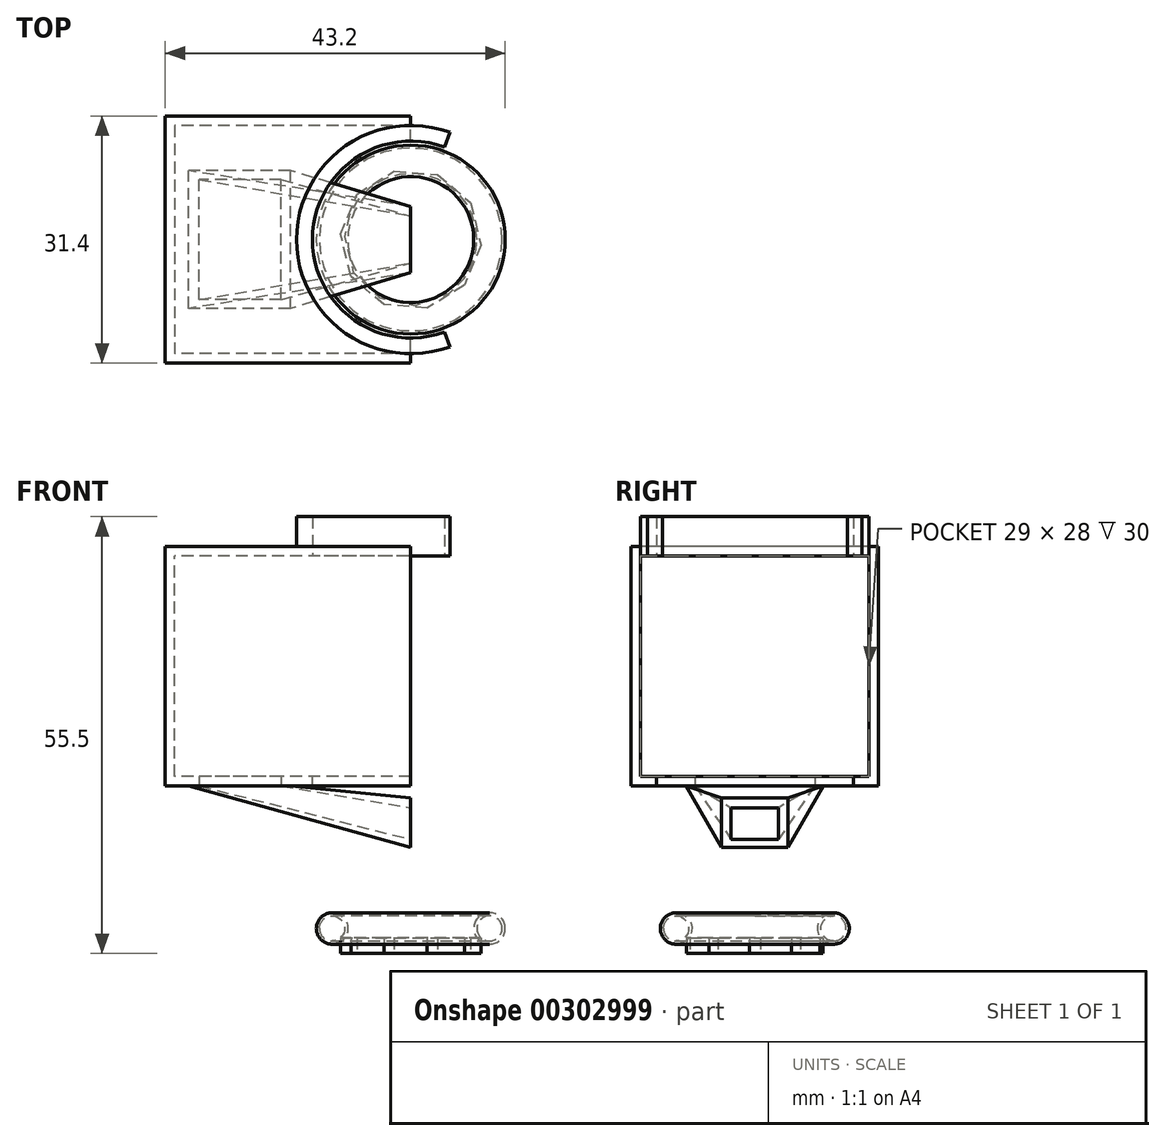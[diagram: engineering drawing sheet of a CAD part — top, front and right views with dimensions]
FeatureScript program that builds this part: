
annotation { "Feature Type Name" : "Feature", "Feature Type Description" : "" }
export const myFeature = defineFeature(function(context is Context, id is Id, definition is map)
    precondition{}
    {
        {
            var Q0;
            Q0=qCreatedBy(makeId("Top.planeOp"),FACE);
            var sketch = newSketch(context, id + "F0", { "sketchPlane" : qUnion([Q0])});
            skCircle(sketch, "E0", {"center": v(0, 0) * mm, "radius": 12.5 * mm});
            skCircle(sketch, "E1", {"center": v(0, 0) * mm, "radius": 14.5 * mm});
            skLineSegment(sketch, "E2.bottom", {"start": v(0, 14.5) * mm, "end": v(-30, 14.5) * mm});
            skLineSegment(sketch, "E2.top", {"start": v(0, -14.5) * mm, "end": v(-30, -14.5) * mm});
            skLineSegment(sketch, "E2.left", {"start": v(0, 14.5) * mm, "end": v(0, -14.5) * mm});
            skLineSegment(sketch, "E2.right", {"start": v(-30, 14.5) * mm, "end": v(-30, -14.5) * mm});
            skLineSegment(sketch, "E3.0", {"start": v(0, -15.7) * mm, "end": v(-31.2, -15.7) * mm});
            skLineSegment(sketch, "E3.1", {"start": v(-31.2, 15.7) * mm, "end": v(-31.2, -15.7) * mm});
            skLineSegment(sketch, "E3.2", {"start": v(0, 15.7) * mm, "end": v(-31.2, 15.7) * mm});
            skLineSegment(sketch, "E4", {"start": v(0, -15.7) * mm, "end": v(0, -14.5) * mm});
            skLineSegment(sketch, "E5", {"start": v(0, 14.5) * mm, "end": v(0, 15.7) * mm});
            skLineSegment(sketch, "E6", {"start": v(0, 0) * mm, "end": v(4.96, 13.63) * mm});
            skLineSegment(sketch, "E7", {"start": v(0, 0) * mm, "end": v(4.96, -13.63) * mm});
            skSolve(sketch);
        }
        {
            var Q0;
            {var subQ0=sQuery(id+"F0.wireOp",EDGE,"E2.left");var subQ1=sQuery(id+"F0.wireOp",EDGE,"E0");var subQ2=makeQuery(id+"F0.imprint","INTERSECT",VERTEX,{"disambiguationData":[OD(0.0)],"derivedFrom":[subQ1,subQ0]});Q0=makeQuery(id+"F0.imprint","IMPRINT",FACE,{"disambiguationData":[TD([[makeQuery(id+"F0.imprint","IMPRINT",EDGE,{"disambiguationData":[TD([[subQ2,-1.0]])],"derivedFrom":subQ1}),-1.0]])]});}
            var Q1;
            {var subQ0=sQuery(id+"F0.wireOp",EDGE,"E2.left");var subQ1=sQuery(id+"F0.wireOp",EDGE,"E0");var subQ2=makeQuery(id+"F0.imprint","INTERSECT",VERTEX,{"disambiguationData":[OD(0.0)],"derivedFrom":[subQ1,subQ0]});Q1=makeQuery(id+"F0.imprint","IMPRINT",FACE,{"disambiguationData":[TD([[makeQuery(id+"F0.imprint","IMPRINT",EDGE,{"disambiguationData":[TD([[subQ2,1.0]])],"derivedFrom":subQ1}),-1.0]])]});}
            var Q2;
            {var subQ0=sQuery(id+"F0.wireOp",EDGE,"E2.left");var subQ1=sQuery(id+"F0.wireOp",EDGE,"E0");var subQ2=makeQuery(id+"F0.imprint","INTERSECT",VERTEX,{"disambiguationData":[OD(1.0)],"derivedFrom":[subQ1,subQ0]});Q2=makeQuery(id+"F0.imprint","IMPRINT",FACE,{"disambiguationData":[TD([[makeQuery(id+"F0.imprint","IMPRINT",EDGE,{"disambiguationData":[TD([[subQ2,-1.0]])],"derivedFrom":subQ1}),-1.0]])]});}
            extrude(context, id + "F1", {"entities" : qUnion([Q0, Q1, Q2]), "depth" : 5 * mm, "offsetDistance" : 25 * mm});
        }
        {
            var Q0;
            {var subQ1=sQuery(id+"F0.wireOp",EDGE,"E2.bottom");Q0=makeQuery(id+"F0.imprint","IMPRINT",FACE,{"disambiguationData":[TD([[makeQuery(id+"F0.imprint","IMPRINT",EDGE,{"derivedFrom":subQ1}),1.0]])]});}
            var Q1;
            Q1=makeQuery(id+"F0.imprint","IMPRINT",FACE,{"disambiguationData":[TD([[makeQuery(id+"F0.imprint","IMPRINT",EDGE,{"derivedFrom":sQuery(id+"F0.wireOp",EDGE,"E2.bottom")}),-1.0]])]});
            extrude(context, id + "F2", {"entities" : qUnion([Q0, Q1]), "operationType" : NewBodyOperationType.ADD, "depth" : 1.2 * mm, "offsetDistance" : 25 * mm});
        }
        {
            var Q0;
            Q0=makeQuery(id+"F0.imprint","IMPRINT",FACE,{"disambiguationData":[TD([[makeQuery(id+"F0.imprint","IMPRINT",EDGE,{"derivedFrom":sQuery(id+"F0.wireOp",EDGE,"E2.bottom")}),-1.0]])]});
            extrude(context, id + "F3", {"entities" : qUnion([Q0]), "operationType" : NewBodyOperationType.ADD, "oppositeDirection" : true, "depth" : 28 * mm, "offsetDistance" : 25 * mm});
        }
        {
            var Q0;
            Q0=makeQuery(id+"F3.opExtrude","CAP_FACE",FACE,{"disambiguationData":[OSD([sQuery(id+"F0.wireOp",EDGE,"E2.bottom"),sQuery(id+"F0.wireOp",EDGE,"E2.top"),sQuery(id+"F0.wireOp",EDGE,"E2.right"),sQuery(id+"F0.wireOp",EDGE,"E3.0"),sQuery(id+"F0.wireOp",EDGE,"E3.1"),sQuery(id+"F0.wireOp",EDGE,"E3.2"),sQuery(id+"F0.wireOp",EDGE,"E4"),sQuery(id+"F0.wireOp",EDGE,"E5")])],"isStart":false});
            var sketch = newSketch(context, id + "F4", { "sketchPlane" : qUnion([Q0])});
            skLineSegment(sketch, "E8.bottom", {"start": v(-31.2, 15.7) * mm, "end": v(0, 15.7) * mm});
            skLineSegment(sketch, "E8.top", {"start": v(-31.2, -15.7) * mm, "end": v(0, -15.7) * mm});
            skLineSegment(sketch, "E8.left", {"start": v(-31.2, 15.7) * mm, "end": v(-31.2, -15.7) * mm});
            skLineSegment(sketch, "E8.right", {"start": v(0, 15.7) * mm, "end": v(0, -15.7) * mm});
            skCircle(sketch, "E9", {"center": v(0, 0) * mm, "radius": 12.5 * mm});
            skSolve(sketch);
        }
        {
            var Q0;
            {var subQ3=sQuery(id+"F4.wireOp",EDGE,"E8.bottom");Q0=makeQuery(id+"F4.imprint","IMPRINT",FACE,{"disambiguationData":[TD([[makeQuery(id+"F4.imprint","IMPRINT",EDGE,{"derivedFrom":subQ3}),1.0]])]});}
            var Q1;
            {var subQ0=makeQuery(id+"F3.opExtrude","CAP_EDGE",EDGE,{"disambiguationData":[OSD([sQuery(id+"F0.wireOp",EDGE,"E2.bottom")])],"isStart":false});Q1=makeQuery(id+"F4.imprint","IMPRINT",FACE,{"disambiguationData":[TD([[makeQuery(id+"F4.imprint","IMPRINT",EDGE,{"derivedFrom":subQ0}),-1.0]])]});}
            extrude(context, id + "F5", {"entities" : qUnion([Q0, Q1]), "operationType" : NewBodyOperationType.ADD, "depth" : 1.2 * mm, "offsetDistance" : 25 * mm});
        }
        {
            var Q0;
            {var subQ0=sQuery(id+"F4.wireOp",EDGE,"E8.right");var subQ1=makeQuery(id+"F4.imprint","INTERSECT",VERTEX,{"derivedFrom":[makeQuery(id+"F3.opExtrude","CAP_EDGE",EDGE,{"disambiguationData":[OSD([sQuery(id+"F0.wireOp",EDGE,"E2.top")])],"isStart":false}),subQ0]});var subQ2=sQuery(id+"F0.wireOp",EDGE,"E4");Q0=makeQuery(id+"F5.boolean.opBoolean","MERGE",FACE,{"derivedFrom":[makeQuery(id+"F3.boolean.opBoolean","MERGE",FACE,{"derivedFrom":[makeQuery(id+"F2.opExtrude","SWEPT_FACE",FACE,{"disambiguationData":[OSD([subQ2])]}),makeQuery(id+"F3.opExtrude","SWEPT_FACE",FACE,{"disambiguationData":[OSD([subQ2])]})]}),makeQuery(id+"F5.opExtrude","SWEPT_FACE",FACE,{"disambiguationData":[OSD([subQ0]),TDD([makeQuery(id+"F4.imprint","IMPRINT",EDGE,{"disambiguationData":[TD([[subQ1,-1.0]])],"derivedFrom":subQ0}),makeQuery(id+"F4.imprint","IMPRINT",EDGE,{"disambiguationData":[TD([[subQ1,1.0]])],"derivedFrom":subQ0})])]})]});}
            var sketch = newSketch(context, id + "F6", { "sketchPlane" : qUnion([Q0])});
            skLineSegment(sketch, "E10", {"start": v(-12.5, -28) * mm, "end": v(0, -28) * mm, "construction": true});
            skLineSegment(sketch, "E11", {"start": v(0, -28) * mm, "end": v(0, -34) * mm, "construction": true});
            skLineSegment(sketch, "E12.bottom", {"start": v(-3, -32) * mm, "end": v(3, -32) * mm});
            skLineSegment(sketch, "E12.top", {"start": v(-3, -36) * mm, "end": v(3, -36) * mm});
            skLineSegment(sketch, "E12.left", {"start": v(-3, -32) * mm, "end": v(-3, -36) * mm});
            skLineSegment(sketch, "E12.right", {"start": v(3, -32) * mm, "end": v(3, -36) * mm});
            skPoint(sketch, "E12.middle", {"position": v(0, -34) * mm});
            skSolve(sketch);
        }
        {
            var Q0;
            Q0=makeQuery(id+"F5.opExtrude","CAP_FACE",FACE,{"disambiguationData":[OSD([sQuery(id+"F4.wireOp",EDGE,"E8.bottom"),sQuery(id+"F4.wireOp",EDGE,"E8.top"),sQuery(id+"F4.wireOp",EDGE,"E8.left"),sQuery(id+"F4.wireOp",EDGE,"E8.right"),sQuery(id+"F4.wireOp",EDGE,"E9")])],"isStart":false});
            var sketch = newSketch(context, id + "F7", { "sketchPlane" : qUnion([Q0])});
            skLineSegment(sketch, "E13", {"start": v(-12.5, 0) * mm, "end": v(-21.66, 0) * mm, "construction": true});
            skLineSegment(sketch, "E14.bottom", {"start": v(-16.46, 7.62) * mm, "end": v(-26.87, 7.62) * mm});
            skLineSegment(sketch, "E14.top", {"start": v(-16.46, -7.62) * mm, "end": v(-26.87, -7.62) * mm});
            skLineSegment(sketch, "E14.left", {"start": v(-16.46, 7.62) * mm, "end": v(-16.46, -7.62) * mm});
            skLineSegment(sketch, "E14.right", {"start": v(-26.87, 7.62) * mm, "end": v(-26.87, -7.62) * mm});
            skPoint(sketch, "E14.middle", {"position": v(-21.66, 0) * mm});
            skSolve(sketch);
        }
        {
            var Q0;
            Q0=makeQuery(id+"F7.imprint","IMPRINT",FACE,{"disambiguationData":[TD([[makeQuery(id+"F7.imprint","IMPRINT",EDGE,{"derivedFrom":sQuery(id+"F7.wireOp",EDGE,"E14.bottom")}),-1.0]])]});
            var sketch = newSketch(context, id + "F8", { "sketchPlane" : qUnion([Q0])});
            skLineSegment(sketch, "E15.bottom", {"start": v(-15.29, 8.75) * mm, "end": v(-28.2, 8.75) * mm});
            skLineSegment(sketch, "E15.top", {"start": v(-15.29, -8.75) * mm, "end": v(-28.2, -8.75) * mm});
            skLineSegment(sketch, "E15.left", {"start": v(-15.29, 8.75) * mm, "end": v(-15.29, -8.75) * mm});
            skLineSegment(sketch, "E15.right", {"start": v(-28.2, 8.75) * mm, "end": v(-28.2, -8.75) * mm});
            skPoint(sketch, "E15.middle", {"position": v(-21.74, 0) * mm});
            skSolve(sketch);
        }
        {
            var Q0;
            {var subQ3=sQuery(id+"F0.wireOp",EDGE,"E4");Q0=makeQuery(id+"F6.imprint","IMPRINT",FACE,{"disambiguationData":[TD([[makeQuery(id+"F6.imprint","IMPRINT",EDGE,{"derivedFrom":makeQuery(id+"F2.opExtrude","CAP_EDGE",EDGE,{"disambiguationData":[OSD([subQ3])],"isStart":false})}),-1.0]])]});}
            var sketch = newSketch(context, id + "F9", { "sketchPlane" : qUnion([Q0])});
            skLineSegment(sketch, "E16.bottom", {"start": v(-4.21, -30.74) * mm, "end": v(4.21, -30.74) * mm});
            skLineSegment(sketch, "E16.top", {"start": v(-4.21, -36.99) * mm, "end": v(4.21, -36.99) * mm});
            skLineSegment(sketch, "E16.left", {"start": v(-4.21, -30.74) * mm, "end": v(-4.21, -36.99) * mm});
            skLineSegment(sketch, "E16.right", {"start": v(4.21, -30.74) * mm, "end": v(4.21, -36.99) * mm});
            skPoint(sketch, "E16.middle", {"position": v(0, -33.87) * mm});
            skSolve(sketch);
        }
        {
            var Q0;
            Q0=makeQuery(id+"F8.imprint","IMPRINT",FACE,{"disambiguationData":[TD([[makeQuery(id+"F8.imprint","IMPRINT",EDGE,{"derivedFrom":makeQuery(id+"F7.imprint","IMPRINT",EDGE,{"derivedFrom":sQuery(id+"F7.wireOp",EDGE,"E14.bottom")})}),1.0]])]});
            extrude(context, id + "F10", {"entities" : qUnion([Q0]), "operationType" : NewBodyOperationType.REMOVE, "oppositeDirection" : true, "depth" : 25 * mm, "offsetDistance" : 25 * mm});
        }
        {
            var Q1;
            Q1 = qSketchRegion(id + "F9", true);
            var Q2;
            Q2 = qSketchRegion(id + "F8", true);
            loft(context, id + "F11", {"operationType" : NewBodyOperationType.ADD, "sheetProfilesArray" : [{ "sheetProfileEntities" : qUnion([Q1]) }, { "sheetProfileEntities" : qUnion([Q2]) }]});
        }
        {
            var Q1;
            Q1 = qSketchRegion(id + "F7", true);
            var Q2;
            Q2 = qSketchRegion(id + "F6", true);
            loft(context, id + "F12", {"operationType" : NewBodyOperationType.REMOVE, "sheetProfilesArray" : [{ "sheetProfileEntities" : qUnion([Q1]) }, { "sheetProfileEntities" : qUnion([Q2]) }]});
        }
        {
            var Q0;
            Q0=qCreatedBy(makeId("Front.planeOp"),FACE);
            var sketch = newSketch(context, id + "F13", { "sketchPlane" : qUnion([Q0])});
            skLineSegment(sketch, "E17", {"start": v(0, -47.31) * mm, "end": v(-10, -47.31) * mm, "construction": true});
            skCircle(sketch, "E18", {"center": v(-10, -47.31) * mm, "radius": 2 * mm});
            skCircle(sketch, "E19", {"center": v(-10, -47.31) * mm, "radius": 1.6 * mm});
            skLineSegment(sketch, "E20", {"start": v(0, -42.12) * mm, "end": v(0, -52.34) * mm, "construction": true});
            skSolve(sketch);
        }
        {
            var Q0;
            Q0=makeQuery(id+"F13.imprint","IMPRINT",FACE,{"disambiguationData":[TD([[makeQuery(id+"F13.imprint","IMPRINT",EDGE,{"derivedFrom":sQuery(id+"F13.wireOp",EDGE,"E18")}),1.0]])]});
            var Q1;
            Q1=sQuery(id+"F13.wireOp",EDGE,"E20");
            revolve(context, id + "F14", {"entities" : qUnion([Q0]), "axis" : qUnion([Q1]), "revolveType" : RevolveType.FULL});
        }
        {
            var Q0;
            Q0=qCreatedBy(makeId("Top.planeOp"),FACE);
            var sketch = newSketch(context, id + "F15", { "sketchPlane" : qUnion([Q0])});
            skCircle(sketch, "E21.cCircle", {"center": v(0, 0) * mm, "radius": 8.5 * mm, "construction": true});
            skLineSegment(sketch, "E21.0", {"start": v(6.8, -5.8) * mm, "end": v(2.1, -8.69) * mm});
            skLineSegment(sketch, "E21.1", {"start": v(2.1, -8.69) * mm, "end": v(-3.41, -8.26) * mm});
            skLineSegment(sketch, "E21.2", {"start": v(-3.41, -8.26) * mm, "end": v(-7.62, -4.68) * mm});
            skLineSegment(sketch, "E21.3", {"start": v(-7.62, -4.68) * mm, "end": v(-8.91, 0.7) * mm});
            skLineSegment(sketch, "E21.4", {"start": v(-8.91, 0.7) * mm, "end": v(-6.8, 5.8) * mm});
            skLineSegment(sketch, "E21.5", {"start": v(-6.8, 5.8) * mm, "end": v(-2.1, 8.69) * mm});
            skLineSegment(sketch, "E21.6", {"start": v(-2.1, 8.69) * mm, "end": v(3.41, 8.26) * mm});
            skLineSegment(sketch, "E21.7", {"start": v(3.41, 8.26) * mm, "end": v(7.62, 4.68) * mm});
            skLineSegment(sketch, "E21.8", {"start": v(7.62, 4.68) * mm, "end": v(8.91, -0.7) * mm});
            skLineSegment(sketch, "E21.9", {"start": v(8.91, -0.7) * mm, "end": v(6.8, -5.8) * mm});
            skPoint(sketch, "E21.0.midPoint", {"position": v(4.45, -7.24) * mm});
            skSolve(sketch);
        }
        {
            var Q0;
            Q0=makeQuery(id+"F15.imprint","IMPRINT",FACE,{"disambiguationData":[TD([[makeQuery(id+"F15.imprint","IMPRINT",EDGE,{"derivedFrom":sQuery(id+"F15.wireOp",EDGE,"E21.0")}),-1.0]])]});
            extrude(context, id + "F16", {"entities" : qUnion([Q0]), "depth" : 2 * mm, "offsetDistance" : 25 * mm});
        }
        {
            var Q0;
            Q0=makeQuery(id+"F16.opExtrude","SWEPT_BODY",BODY,{"disambiguationData":[OSD([sQuery(id+"F15.wireOp",EDGE,"E21.0"),sQuery(id+"F15.wireOp",EDGE,"E21.1"),sQuery(id+"F15.wireOp",EDGE,"E21.2"),sQuery(id+"F15.wireOp",EDGE,"E21.3"),sQuery(id+"F15.wireOp",EDGE,"E21.4"),sQuery(id+"F15.wireOp",EDGE,"E21.5"),sQuery(id+"F15.wireOp",EDGE,"E21.6"),sQuery(id+"F15.wireOp",EDGE,"E21.7"),sQuery(id+"F15.wireOp",EDGE,"E21.8"),sQuery(id+"F15.wireOp",EDGE,"E21.9")])]});
            transform(context, id + "F17", {"entities" : qUnion([Q0]), "transformType" : TransformType.TRANSLATION_3D, "dx" : 0 * mm, "dy" : 0 * mm, "dz" : -50.5 * mm, "makeCopy" : false});
        }
    });
